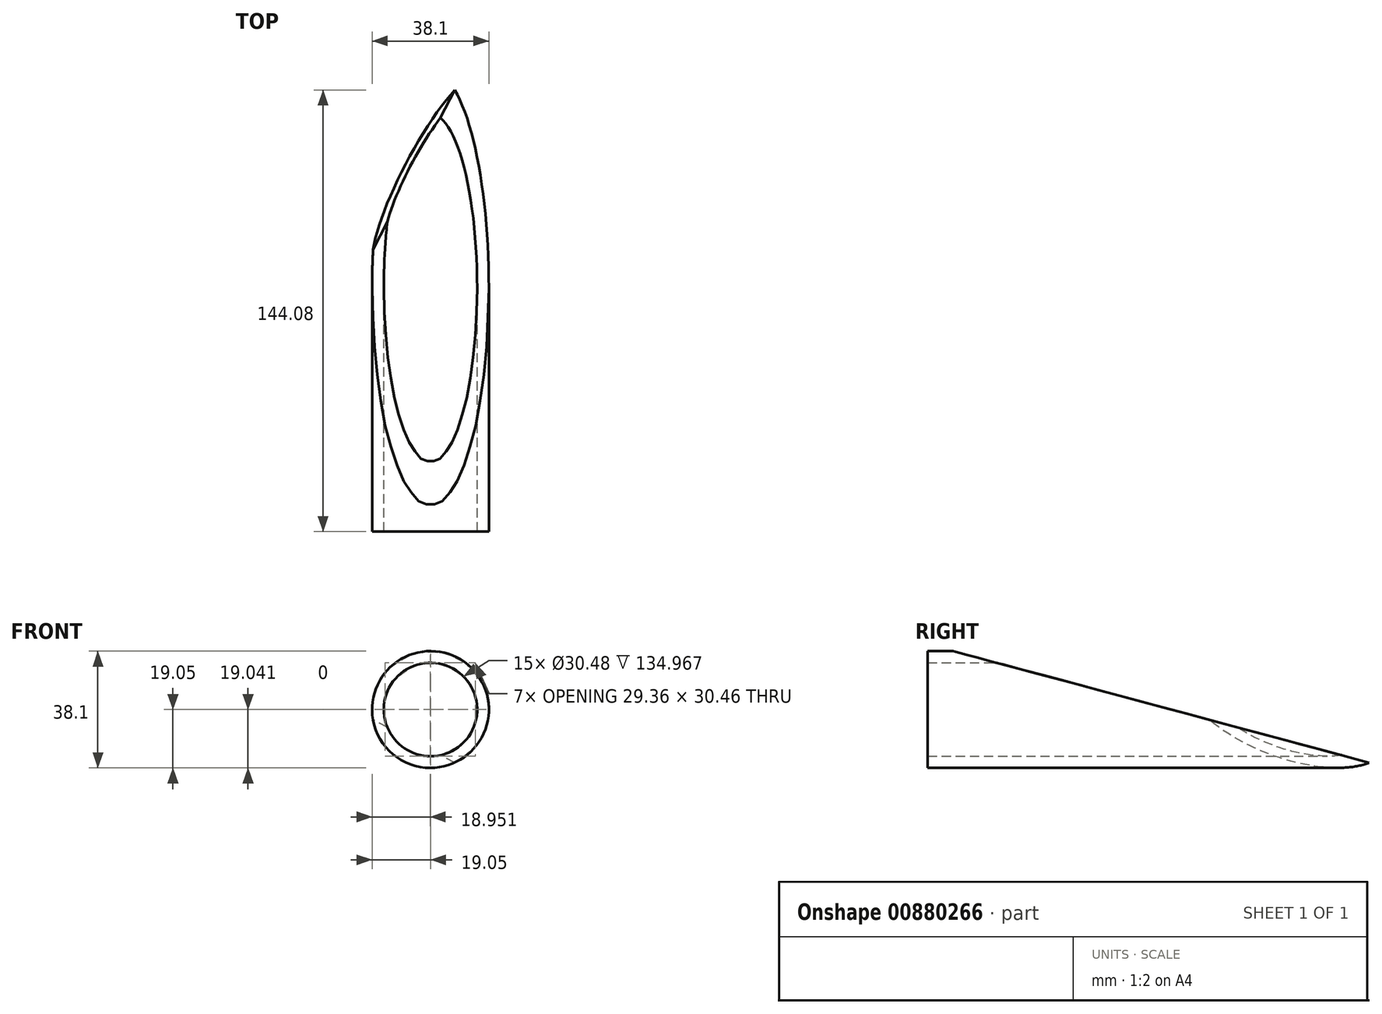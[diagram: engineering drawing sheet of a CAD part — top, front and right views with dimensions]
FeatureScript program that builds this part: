
annotation { "Feature Type Name" : "Feature", "Feature Type Description" : "" }
export const myFeature = defineFeature(function(context is Context, id is Id, definition is map)
    precondition{}
    {
        {
            var Q0;
            Q0=qCreatedBy(makeId("Front.planeOp"),FACE);
            var sketch = newSketch(context, id + "F0", { "sketchPlane" : qUnion([Q0])});
            skCircle(sketch, "E0", {"center": v(0, 0) * mm, "radius": 19.05 * mm});
            skCircle(sketch, "E1", {"center": v(0, 0) * mm, "radius": 15.24 * mm});
            skSolve(sketch);
        }
        {
            var Q0;
            Q0 = qSketchRegion(id + "F0", true);
            extrude(context, id + "F1", {"entities" : qUnion([Q0]), "depth" : 152.4 * mm, "offsetDistance" : 25.4 * mm});
        }
        {
            var Q0;
            Q0=qCreatedBy(makeId("Right.planeOp"),FACE);
            var sketch = newSketch(context, id + "F2", { "sketchPlane" : qUnion([Q0])});
            skLineSegment(sketch, "E2", {"start": v(0, -19.56) * mm, "end": v(-176.7, 27.79) * mm});
            skLineSegment(sketch, "E3", {"start": v(-176.7, 27.79) * mm, "end": v(0, 27.79) * mm});
            skLineSegment(sketch, "E4", {"start": v(0, 27.79) * mm, "end": v(0, -19.56) * mm});
            skSolve(sketch);
        }
        {
            var Q0;
            Q0 = qSketchRegion(id + "F2", true);
            extrude(context, id + "F3", {"entities" : qUnion([Q0]), "operationType" : NewBodyOperationType.REMOVE, "oppositeDirection" : true, "depth" : 50.8 * mm, "offsetDistance" : 25.4 * mm, "symmetric" : true});
        }
        {
            var Q0;
            Q0=qCreatedBy(makeId("Right.planeOp"),FACE);
            var sketch = newSketch(context, id + "F4", { "sketchPlane" : qUnion([Q0])});
            skLineSegment(sketch, "E5", {"start": v(0, 0) * mm, "end": v(-36.98, 0) * mm});
            skSolve(sketch);
        }
        {
            var Q0;
            Q0=qCreatedBy(makeId("Right.planeOp"),FACE);
            var Q1;
            Q1=sQuery(id+"F4.wireOp",EDGE,"E5");
            cPlane(context, id + "F5", {"entities" : qUnion([Q0, Q1]), "cplaneType" : CPlaneType.LINE_ANGLE, "offset" : 25.4 * mm, "angle" : 60 * degree, "width" : 152.4 * mm, "height" : 152.4 * mm});
        }
        {
            var Q0;
            Q0=qCreatedBy(id+"F5.planeOp",FACE);
            var sketch = newSketch(context, id + "F6", { "sketchPlane" : qUnion([Q0])});
            skLineSegment(sketch, "E6", {"start": v(20.32, 0) * mm, "end": v(-100.01, 208.42) * mm});
            skLineSegment(sketch, "E7", {"start": v(-100.01, 208.42) * mm, "end": v(-100.01, 0) * mm});
            skLineSegment(sketch, "E8", {"start": v(-100.01, 0) * mm, "end": v(20.32, 0) * mm});
            skSolve(sketch);
        }
        {
            var Q0;
            Q0 = qSketchRegion(id + "F6", true);
            extrude(context, id + "F7", {"entities" : qUnion([Q0]), "operationType" : NewBodyOperationType.REMOVE, "endBound" : BoundingType.THROUGH_ALL, "depth" : 25.4 * mm, "offsetDistance" : 25.4 * mm});
        }
    });
